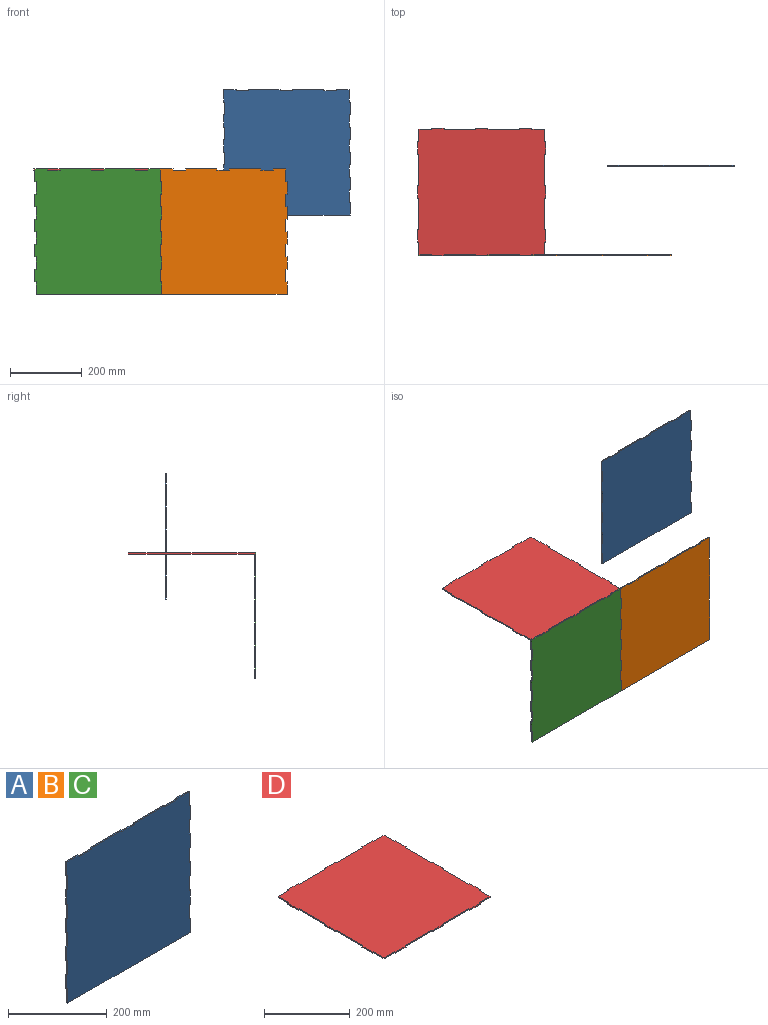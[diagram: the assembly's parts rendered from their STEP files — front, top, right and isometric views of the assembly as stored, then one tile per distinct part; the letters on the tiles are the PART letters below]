
ASSEMBLY  parts=4 mates=2
PART A: 54 faces, bbox 353x3x350 mm
  f0: plane 3x3mm, normal (0,0,1), area 9mm2, adj f1,f51,f52,f53
  f1: plane 35x3mm, normal (1,0,0), area 105mm2, adj f0,f2,f52,f53
  f2: plane 3x3mm, normal (0,0,-1), area 9mm2, adj f1,f3,f52,f53
  f3: plane 35x3mm, normal (1,0,0), area 105mm2, adj f2,f4,f52,f53
  f4: plane 3x3mm, normal (0,0,1), area 9mm2, adj f3,f5,f52,f53
  f5: plane 35x3mm, normal (1,0,0), area 105mm2, adj f4,f6,f52,f53
  f6: plane 3x3mm, normal (0,0,-1), area 9mm2, adj f5,f7,f52,f53
  f7: plane 35x3mm, normal (1,0,0), area 105mm2, adj f6,f8,f52,f53
  f8: plane 3x3mm, normal (0,0,1), area 9mm2, adj f7,f9,f52,f53
  f9: plane 35x3mm, normal (1,0,0), area 105mm2, adj f8,f10,f52,f53
  f10: plane 3x3mm, normal (0,0,-1), area 9mm2, adj f9,f11,f52,f53
  f11: plane 35x3mm, normal (1,0,0), area 105mm2, adj f10,f12,f52,f53
  f12: plane 3x3mm, normal (0,0,1), area 9mm2, adj f11,f13,f52,f53
  f13: plane 35x3mm, normal (1,0,0), area 105mm2, adj f12,f14,f52,f53
  f14: plane 3x3mm, normal (0,0,-1), area 9mm2, adj f13,f15,f52,f53
  f15: plane 35x3mm, normal (1,0,0), area 105mm2, adj f14,f16,f52,f53
  f16: plane 3x3mm, normal (0,0,1), area 9mm2, adj f15,f17,f52,f53
  f17: plane 35x3mm, normal (1,0,0), area 105mm2, adj f16,f18,f52,f53
  f18: plane 35x3mm, normal (0,0,1), area 105mm2, adj f17,f19,f52,f53
  f19: plane 3x3mm, normal (-1,0,0), area 9mm2, adj f18,f20,f52,f53
  f20: plane 35x3mm, normal (0,0,1), area 105mm2, adj f19,f21,f52,f53
  f21: plane 3x3mm, normal (1,0,0), area 9mm2, adj f20,f22,f52,f53
  f22: plane 87.5x3mm, normal (0,0,1), area 262.5mm2, adj f21,f23,f52,f53
  f23: plane 3x3mm, normal (-1,0,0), area 9mm2, adj f22,f24,f52,f53
  f24: plane 35x3mm, normal (0,0,1), area 105mm2, adj f23,f25,f52,f53
  f25: plane 3x3mm, normal (1,0,0), area 9mm2, adj f24,f26,f52,f53
  f26: plane 87.5x3mm, normal (0,0,1), area 262.5mm2, adj f25,f27,f52,f53
  f27: plane 3x3mm, normal (-1,0,0), area 9mm2, adj f26,f28,f52,f53
  f28: plane 35x3mm, normal (0,0,1), area 105mm2, adj f27,f29,f52,f53
  f29: plane 3x3mm, normal (1,0,0), area 9mm2, adj f28,f30,f52,f53
  f30: plane 35x3mm, normal (0,0,1), area 105mm2, adj f29,f31,f52,f53
  f31: plane 35x3mm, normal (-1,0,0), area 105mm2, adj f30,f32,f52,f53
  f32: plane 3x3mm, normal (0,0,-1), area 9mm2, adj f31,f33,f52,f53
  f33: plane 35x3mm, normal (-1,0,0), area 105mm2, adj f32,f34,f52,f53
  f34: plane 3x3mm, normal (0,0,1), area 9mm2, adj f33,f35,f52,f53
  f35: plane 35x3mm, normal (-1,0,0), area 105mm2, adj f34,f36,f52,f53
  f36: plane 3x3mm, normal (0,0,-1), area 9mm2, adj f35,f37,f52,f53
  f37: plane 35x3mm, normal (-1,0,0), area 105mm2, adj f36,f38,f52,f53
  f38: plane 3x3mm, normal (0,0,1), area 9mm2, adj f37,f39,f52,f53
  f39: plane 35x3mm, normal (-1,0,0), area 105mm2, adj f38,f40,f52,f53
  f40: plane 3x3mm, normal (0,0,-1), area 9mm2, adj f39,f41,f52,f53
  f41: plane 35x3mm, normal (-1,0,0), area 105mm2, adj f40,f42,f52,f53
  f42: plane 3x3mm, normal (0,0,1), area 9mm2, adj f41,f43,f52,f53
  f43: plane 35x3mm, normal (-1,0,0), area 105mm2, adj f42,f44,f52,f53
  f44: plane 3x3mm, normal (0,0,-1), area 9mm2, adj f43,f45,f52,f53
  f45: plane 35x3mm, normal (-1,0,0), area 105mm2, adj f44,f46,f52,f53
  f46: plane 3x3mm, normal (0,0,1), area 9mm2, adj f45,f47,f52,f53
  f47: plane 35x3mm, normal (-1,0,0), area 105mm2, adj f46,f48,f52,f53
  f48: plane 3x3mm, normal (0,0,-1), area 9mm2, adj f47,f49,f52,f53
  f49: plane 35x3mm, normal (-1,0,0), area 105mm2, adj f48,f50,f52,f53
  f50: plane 350x3mm, normal (0,0,-1), area 1050mm2, adj f49,f51,f52,f53
  f51: plane 35x3mm, normal (1,0,0), area 105mm2, adj f0,f50,f52,f53
  f52: plane 353x350mm, normal (0,-1,0), area 122185mm2, adj f0,f1,f2,f3,f4,f5,f6,f7
  f53: plane 353x350mm, normal (0,1,0), area 122185mm2, adj f0,f1,f2,f3,f4,f5,f6,f7
PART B: same geometry as A
PART C: same geometry as A
PART D: 54 faces, bbox 356x356x3 mm
  f0: plane 35x3mm, normal (0,1,0), area 105mm2, adj f1,f51,f52,f53
  f1: plane 3x3mm, normal (-1,0,0), area 9mm2, adj f0,f2,f52,f53
  f2: plane 87.5x3mm, normal (0,1,0), area 262.5mm2, adj f1,f3,f52,f53
  f3: plane 3x3mm, normal (1,0,0), area 9mm2, adj f2,f4,f52,f53
  f4: plane 35x3mm, normal (0,1,0), area 105mm2, adj f3,f5,f52,f53
  f5: plane 3x3mm, normal (-1,0,0), area 9mm2, adj f4,f6,f52,f53
  f6: plane 87.5x3mm, normal (0,1,0), area 262.5mm2, adj f5,f7,f52,f53
  f7: plane 3x3mm, normal (1,0,0), area 9mm2, adj f6,f8,f52,f53
  f8: plane 35x3mm, normal (0,1,0), area 105mm2, adj f7,f9,f52,f53
  f9: plane 3x3mm, normal (-1,0,0), area 9mm2, adj f8,f10,f52,f53
  f10: plane 35x3mm, normal (0,1,0), area 105mm2, adj f9,f11,f52,f53
  f11: plane 35x3mm, normal (-1,0,0), area 105mm2, adj f10,f12,f52,f53
  f12: plane 3x3mm, normal (0,1,0), area 9mm2, adj f11,f13,f52,f53
  f13: plane 35x3mm, normal (-1,0,0), area 105mm2, adj f12,f14,f52,f53
  f14: plane 3x3mm, normal (0,-1,0), area 9mm2, adj f13,f15,f52,f53
  f15: plane 87.5x3mm, normal (-1,0,0), area 262.5mm2, adj f14,f16,f52,f53
  f16: plane 3x3mm, normal (0,1,0), area 9mm2, adj f15,f17,f52,f53
  f17: plane 35x3mm, normal (-1,0,0), area 105mm2, adj f16,f18,f52,f53
  f18: plane 3x3mm, normal (0,-1,0), area 9mm2, adj f17,f19,f52,f53
  f19: plane 87.5x3mm, normal (-1,0,0), area 262.5mm2, adj f18,f20,f52,f53
  f20: plane 3x3mm, normal (0,1,0), area 9mm2, adj f19,f21,f52,f53
  f21: plane 35x3mm, normal (-1,0,0), area 105mm2, adj f20,f22,f52,f53
  f22: plane 3x3mm, normal (0,-1,0), area 9mm2, adj f21,f23,f52,f53
  f23: plane 35x3mm, normal (-1,0,0), area 105mm2, adj f22,f24,f52,f53
  f24: plane 35x3mm, normal (0,-1,0), area 105mm2, adj f23,f25,f52,f53
  f25: plane 3x3mm, normal (-1,0,0), area 9mm2, adj f24,f26,f52,f53
  f26: plane 35x3mm, normal (0,-1,0), area 105mm2, adj f25,f27,f52,f53
  f27: plane 3x3mm, normal (1,0,0), area 9mm2, adj f26,f28,f52,f53
  f28: plane 87.5x3mm, normal (0,-1,0), area 262.5mm2, adj f27,f29,f52,f53
  f29: plane 3x3mm, normal (-1,0,0), area 9mm2, adj f28,f30,f52,f53
  f30: plane 35x3mm, normal (0,-1,0), area 105mm2, adj f29,f31,f52,f53
  f31: plane 3x3mm, normal (1,0,0), area 9mm2, adj f30,f32,f52,f53
  f32: plane 87.5x3mm, normal (0,-1,0), area 262.5mm2, adj f31,f33,f52,f53
  f33: plane 3x3mm, normal (-1,0,0), area 9mm2, adj f32,f34,f52,f53
  f34: plane 35x3mm, normal (0,-1,0), area 105mm2, adj f33,f35,f52,f53
  f35: plane 3x3mm, normal (1,0,0), area 9mm2, adj f34,f36,f52,f53
  f36: plane 35x3mm, normal (0,-1,0), area 105mm2, adj f35,f37,f52,f53
  f37: plane 35x3mm, normal (1,0,0), area 105mm2, adj f36,f38,f52,f53
  f38: plane 3x3mm, normal (0,-1,0), area 9mm2, adj f37,f39,f52,f53
  f39: plane 35x3mm, normal (1,0,0), area 105mm2, adj f38,f40,f52,f53
  f40: plane 3x3mm, normal (0,1,0), area 9mm2, adj f39,f41,f52,f53
  f41: plane 87.5x3mm, normal (1,0,0), area 262.5mm2, adj f40,f42,f52,f53
  f42: plane 3x3mm, normal (0,-1,0), area 9mm2, adj f41,f43,f52,f53
  f43: plane 35x3mm, normal (1,0,0), area 105mm2, adj f42,f44,f52,f53
  f44: plane 3x3mm, normal (0,1,0), area 9mm2, adj f43,f45,f52,f53
  f45: plane 87.5x3mm, normal (1,0,0), area 262.5mm2, adj f44,f46,f52,f53
  f46: plane 3x3mm, normal (0,-1,0), area 9mm2, adj f45,f47,f52,f53
  f47: plane 35x3mm, normal (1,0,0), area 105mm2, adj f46,f48,f52,f53
  f48: plane 3x3mm, normal (0,1,0), area 9mm2, adj f47,f49,f52,f53
  f49: plane 35x3mm, normal (1,0,0), area 105mm2, adj f48,f50,f52,f53
  f50: plane 35x3mm, normal (0,1,0), area 105mm2, adj f49,f51,f52,f53
  f51: plane 3x3mm, normal (1,0,0), area 9mm2, adj f0,f50,f52,f53
  f52: plane 356x356mm, normal (0,0,1), area 123760mm2, adj f0,f1,f2,f3,f4,f5,f6,f7
  f53: plane 356x356mm, normal (0,0,-1), area 123760mm2, adj f0,f1,f2,f3,f4,f5,f6,f7
PLACE A t=(447.96,366.47,158.21)mm
PLACE B t=(272.08,117.27,-63.27)mm
PLACE C t=(-77.92,117.27,-63.27)mm
PLACE D t=(-77.92,292.27,108.73)mm
MATE fastened D.f33 <-> C.f21  axis (-1,0,0) through (27.08,115.77,110.23)mm
MATE fastened C.f15 <-> B.f33  axis (1,0,0) through (100.08,115.77,59.23)mm
